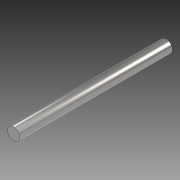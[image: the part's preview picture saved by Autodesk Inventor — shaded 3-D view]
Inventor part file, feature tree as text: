
AUTODESK INVENTOR PART (.ipt)
format: ipt  version: 2020 (Build 240168000, 168)  size: 76,800 bytes
history: native  units: mm
features: extrude x1, sketch x1
ambient origin geometry x8: Origin, YZ Plane, XZ Plane, XY Plane, X Axis, Y Axis, Z Axis, Center Point
bodies: Solid1 (feature_tree)
feature tree (2):
  extrude  "Extrusion1"  Depth=210.0mm TaperAngle=0.0deg
  sketch  "Sketch1"  dims[d0=17.0mm d1=210.0mm d2=0.0mm]
